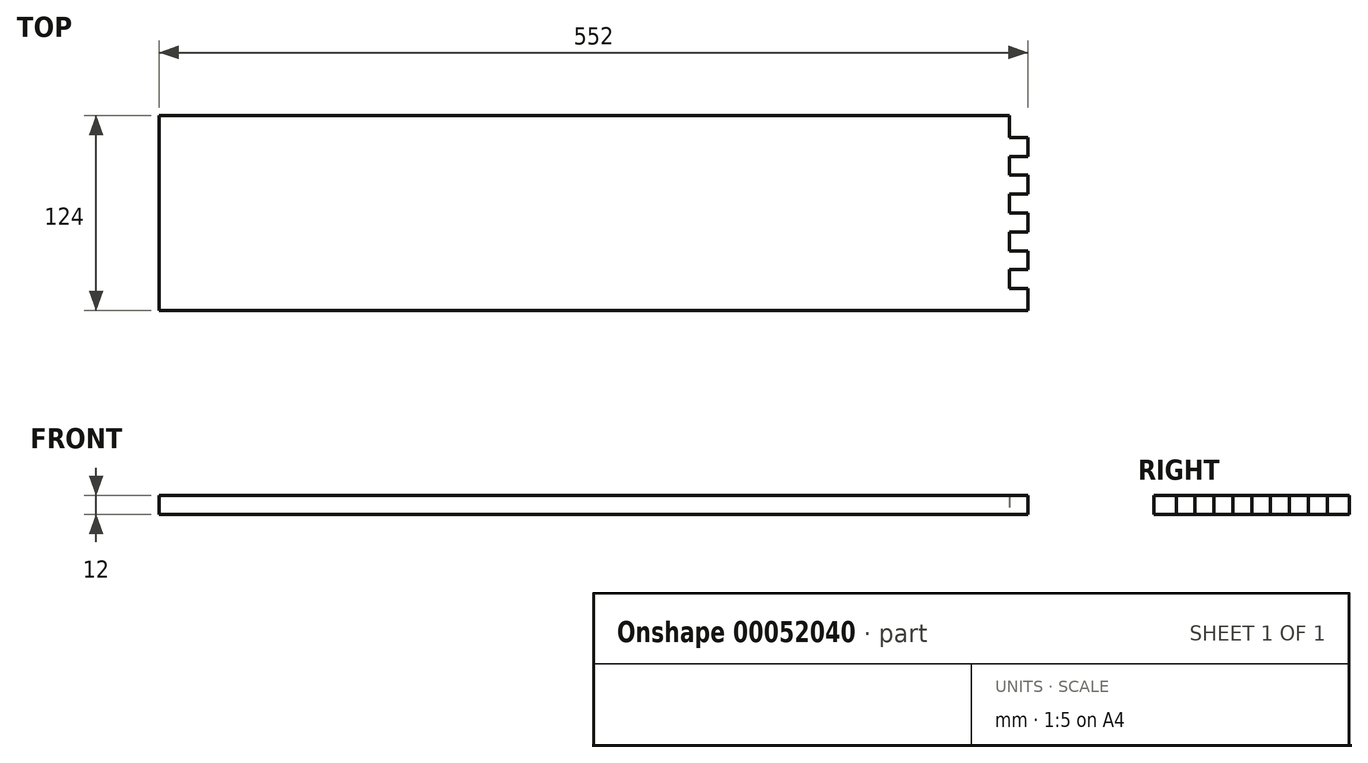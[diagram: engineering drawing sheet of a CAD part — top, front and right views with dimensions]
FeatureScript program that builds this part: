
annotation { "Feature Type Name" : "Feature", "Feature Type Description" : "" }
export const myFeature = defineFeature(function(context is Context, id is Id, definition is map)
    precondition{}
    {
        {
            var Q0;
            Q0=qCreatedBy(makeId("Top.planeOp"),FACE);
            var sketch = newSketch(context, id + "F0", { "sketchPlane" : qUnion([Q0])});
            skLineSegment(sketch, "E0.rect.bottom", {"start": v(276, 62) * mm, "end": v(-276, 62) * mm, "construction": true});
            skLineSegment(sketch, "E0.rect.top", {"start": v(276, -62) * mm, "end": v(-276, -62) * mm, "construction": true});
            skLineSegment(sketch, "E0.rect.left", {"start": v(276, 62) * mm, "end": v(276, -62) * mm, "construction": true});
            skLineSegment(sketch, "E0.rect.right", {"start": v(-276, 62) * mm, "end": v(-276, -62) * mm});
            skPoint(sketch, "E0.rect.middle", {"position": v(0, 0) * mm});
            skLineSegment(sketch, "E1", {"start": v(264, -62) * mm, "end": v(264, 62) * mm, "construction": true});
            skLineSegment(sketch, "E2", {"start": v(-276, -62) * mm, "end": v(276, -62) * mm});
            skLineSegment(sketch, "E3", {"start": v(276, -48) * mm, "end": v(264, -48) * mm});
            skLineSegment(sketch, "E4", {"start": v(264, -48) * mm, "end": v(264, -36) * mm});
            skLineSegment(sketch, "E5", {"start": v(264, -36) * mm, "end": v(276, -36) * mm});
            skLineSegment(sketch, "E6", {"start": v(276, -36) * mm, "end": v(276, -24) * mm});
            skLineSegment(sketch, "E7", {"start": v(276, -24) * mm, "end": v(264, -24) * mm});
            skLineSegment(sketch, "E8", {"start": v(264, -24) * mm, "end": v(264, -12) * mm});
            skLineSegment(sketch, "E9", {"start": v(264, -12) * mm, "end": v(276, -12) * mm});
            skLineSegment(sketch, "E10", {"start": v(276, -12) * mm, "end": v(276, 0) * mm});
            skLineSegment(sketch, "E11", {"start": v(276, -48) * mm, "end": v(276, -62) * mm});
            skLineSegment(sketch, "E12", {"start": v(276, 0) * mm, "end": v(264, 0) * mm});
            skLineSegment(sketch, "E13", {"start": v(264, 0) * mm, "end": v(264, 12) * mm});
            skLineSegment(sketch, "E14", {"start": v(264, 12) * mm, "end": v(276, 12) * mm});
            skLineSegment(sketch, "E15", {"start": v(276, 12) * mm, "end": v(276, 24) * mm});
            skLineSegment(sketch, "E16", {"start": v(276, 24) * mm, "end": v(264, 24) * mm});
            skLineSegment(sketch, "E17", {"start": v(264, 24) * mm, "end": v(264, 36) * mm});
            skLineSegment(sketch, "E18", {"start": v(264, 36) * mm, "end": v(276, 36) * mm});
            skLineSegment(sketch, "E19", {"start": v(276, 36) * mm, "end": v(276, 48) * mm});
            skLineSegment(sketch, "E20", {"start": v(276, 48) * mm, "end": v(264, 48) * mm});
            skLineSegment(sketch, "E21", {"start": v(264, 62) * mm, "end": v(264, 48) * mm});
            skLineSegment(sketch, "E22", {"start": v(264, 62) * mm, "end": v(-276, 62) * mm});
            skSolve(sketch);
        }
        {
            var Q0;
            Q0=qSketchRegion(id+"F0",true);
            extrude(context, id + "F1", {"entities" : qUnion([Q0]), "depth" : 12 * mm});
        }
    });
